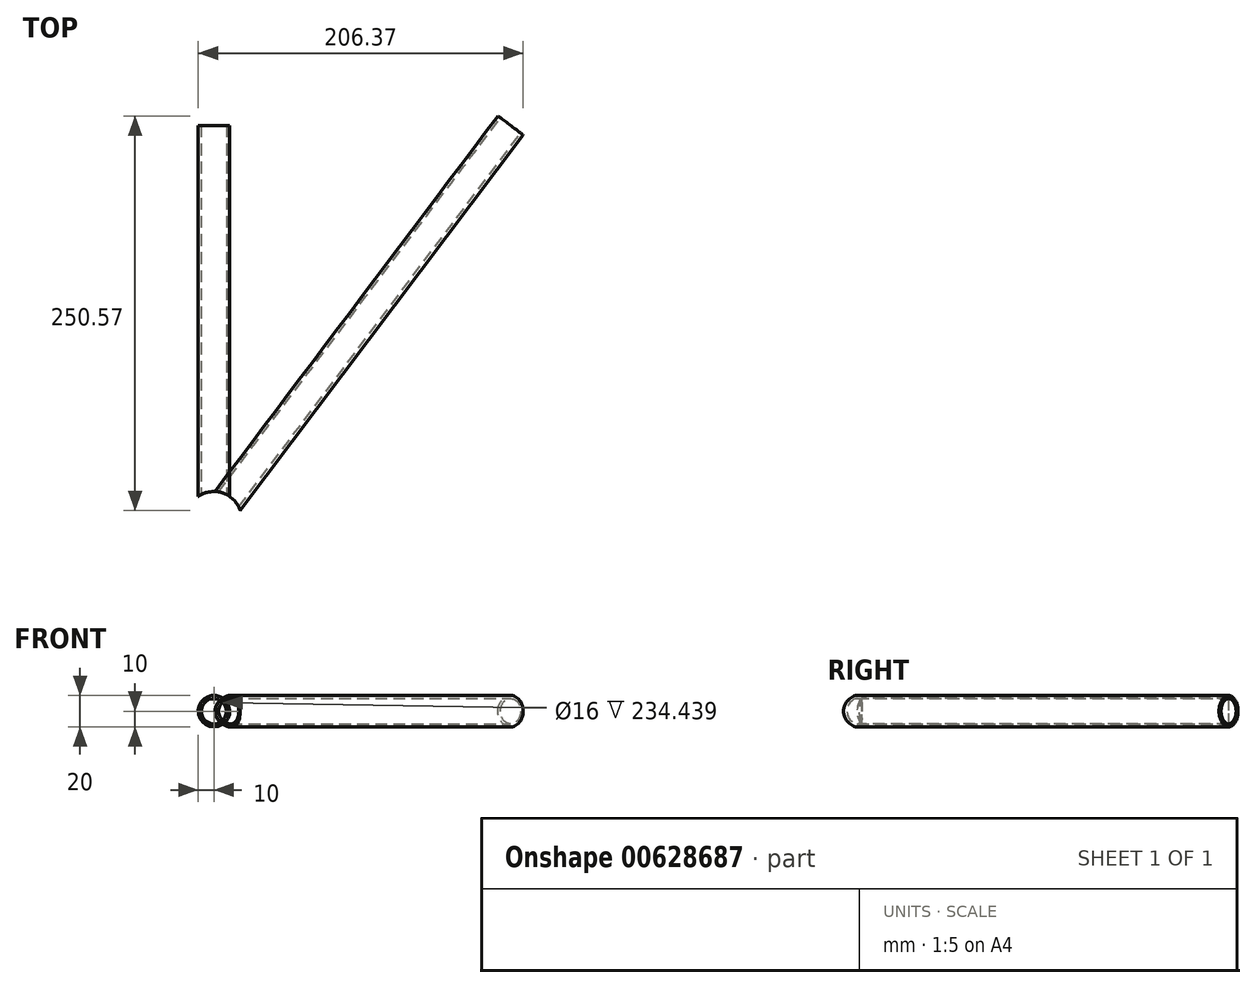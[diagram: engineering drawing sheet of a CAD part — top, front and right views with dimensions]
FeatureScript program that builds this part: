
annotation { "Feature Type Name" : "Feature", "Feature Type Description" : "" }
export const myFeature = defineFeature(function(context is Context, id is Id, definition is map)
    precondition{}
    {
        {
            var Q0;
            Q0=qCreatedBy(makeId("Top.planeOp"),FACE);
            var sketch = newSketch(context, id + "F0", { "sketchPlane" : qUnion([Q0])});
            skLineSegment(sketch, "E0", {"start": v(0, 0) * mm, "end": v(0, 250) * mm, "construction": true});
            skLineSegment(sketch, "E1", {"start": v(0, 0) * mm, "end": v(188.39, 250) * mm, "construction": true});
            skLineSegment(sketch, "E2", {"start": v(188.39, 250) * mm, "end": v(0, 250) * mm, "construction": true});
            skCircle(sketch, "E3", {"center": v(0, 0) * mm, "radius": 17.5 * mm, "construction": true});
            skSolve(sketch);
        }
        {
            var Q0;
            Q0=qCreatedBy(makeId("Right.planeOp"),FACE);
            var sketch = newSketch(context, id + "F1", { "sketchPlane" : qUnion([Q0])});
            skLineSegment(sketch, "E4", {"start": v(-17.5, 10) * mm, "end": v(-17.5, -10) * mm});
            skLineSegment(sketch, "E5", {"start": v(-17.5, -10) * mm, "end": v(-13.5, -10) * mm});
            skLineSegment(sketch, "E6", {"start": v(-13.5, -10) * mm, "end": v(-13.5, -8) * mm});
            skLineSegment(sketch, "E7", {"start": v(-13.5, -8) * mm, "end": v(-15, -8) * mm});
            skLineSegment(sketch, "E8", {"start": v(-15, -8) * mm, "end": v(-15, 8) * mm});
            skLineSegment(sketch, "E9", {"start": v(-15, 8) * mm, "end": v(-16, 8) * mm});
            skLineSegment(sketch, "E10", {"start": v(-16, 8) * mm, "end": v(-16, 9) * mm});
            skLineSegment(sketch, "E11", {"start": v(-16, 9) * mm, "end": v(-15, 9) * mm});
            skLineSegment(sketch, "E12", {"start": v(-15, 9) * mm, "end": v(-15, 10) * mm});
            skLineSegment(sketch, "E13", {"start": v(-15, 10) * mm, "end": v(-17.5, 10) * mm});
            skLineSegment(sketch, "E14", {"start": v(0, 0) * mm, "end": v(-15, 0) * mm});
            skLineSegment(sketch, "E15", {"start": v(0, 0) * mm, "end": v(0, 7) * mm, "construction": true});
            skLineSegment(sketch, "E16", {"start": v(-15, 0) * mm, "end": v(-17.5, 0) * mm, "construction": true});
            skSolve(sketch);
        }
        {
            var Q0;
            Q0=makeQuery(id+"F1.imprint","IMPRINT",FACE,{"disambiguationData":[TD([[makeQuery(id+"F1.imprint","IMPRINT",EDGE,{"derivedFrom":sQuery(id+"F1.wireOp",EDGE,"E4")}),1.0]])]});
            var Q1;
            Q1=sQuery(id+"F1.wireOp",EDGE,"E15");
            revolve(context, id + "F2", {"entities" : qUnion([Q0]), "axis" : qUnion([Q1]), "revolveType" : RevolveType.FULL});
        }
        {
            var Q0;
            Q0=qCreatedBy(makeId("Front.planeOp"),FACE);
            var sketch = newSketch(context, id + "F3", { "sketchPlane" : qUnion([Q0])});
            skCircle(sketch, "E17", {"center": v(0, 0) * mm, "radius": 10 * mm});
            skCircle(sketch, "E18", {"center": v(0, 0) * mm, "radius": 8 * mm});
            skSolve(sketch);
        }
        {
            var Q0;
            Q0 = qSketchRegion(id + "F3", true);
            var Q1;
            Q1=sQuery(id+"F0.wireOp",VERTEX,"E2.end");
            extrude(context, id + "F4", {"entities" : qUnion([Q0]), "endBound" : BoundingType.UP_TO_VERTEX, "oppositeDirection" : true, "depth" : 25 * mm, "endBoundEntityVertex" : qUnion([Q1]), "offsetDistance" : 25 * mm});
        }
        {
            var Q0;
            Q0=qCreatedBy(makeId("Top.planeOp"),FACE);
            var sketch = newSketch(context, id + "F5", { "sketchPlane" : qUnion([Q0])});
            skCircle(sketch, "E19", {"center": v(0, 0) * mm, "radius": 17.5 * mm});
            skSolve(sketch);
        }
        {
            var Q0;
            Q0 = qSketchRegion(id + "F5", true);
            extrude(context, id + "F6", {"entities" : qUnion([Q0]), "operationType" : NewBodyOperationType.REMOVE, "endBound" : BoundingType.SYMMETRIC, "oppositeDirection" : true, "depth" : 25 * mm, "offsetDistance" : 25 * mm});
        }
        {
            var Q0;
            Q0=qCreatedBy(makeId("Top.planeOp"),FACE);
            var sketch = newSketch(context, id + "F7", { "sketchPlane" : qUnion([Q0])});
            skLineSegment(sketch, "E20", {"start": v(0, 0) * mm, "end": v(7.99, -6.02) * mm, "construction": true});
            skLineSegment(sketch, "E21", {"start": v(7.99, -6.02) * mm, "end": v(196.37, 243.98) * mm});
            skLineSegment(sketch, "E22", {"start": v(196.37, 243.98) * mm, "end": v(188.39, 250) * mm, "construction": true});
            skLineSegment(sketch, "E23", {"start": v(188.39, 250) * mm, "end": v(0, 0) * mm, "construction": true});
            skLineSegment(sketch, "E24", {"start": v(6.39, -4.81) * mm, "end": v(194.78, 245.19) * mm});
            skLineSegment(sketch, "E25", {"start": v(6.39, -4.81) * mm, "end": v(7.99, -6.02) * mm});
            skLineSegment(sketch, "E26", {"start": v(194.78, 245.19) * mm, "end": v(196.37, 243.98) * mm});
            skSolve(sketch);
        }
        {
            var Q0;
            Q0=makeQuery(id+"F7.imprint","IMPRINT",FACE,{"disambiguationData":[TD([[makeQuery(id+"F7.imprint","IMPRINT",EDGE,{"derivedFrom":sQuery(id+"F7.wireOp",EDGE,"E21")}),1.0]])]});
            var Q1;
            Q1=sQuery(id+"F7.wireOp",EDGE,"E23");
            revolve(context, id + "F8", {"entities" : qUnion([Q0]), "axis" : qUnion([Q1]), "revolveType" : RevolveType.FULL});
        }
        {
            var Q0;
            Q0 = qSketchRegion(id + "F5", true);
            extrude(context, id + "F9", {"entities" : qUnion([Q0]), "operationType" : NewBodyOperationType.REMOVE, "endBound" : BoundingType.SYMMETRIC, "oppositeDirection" : true, "depth" : 91.2 * mm, "offsetDistance" : 25 * mm});
        }
    });
